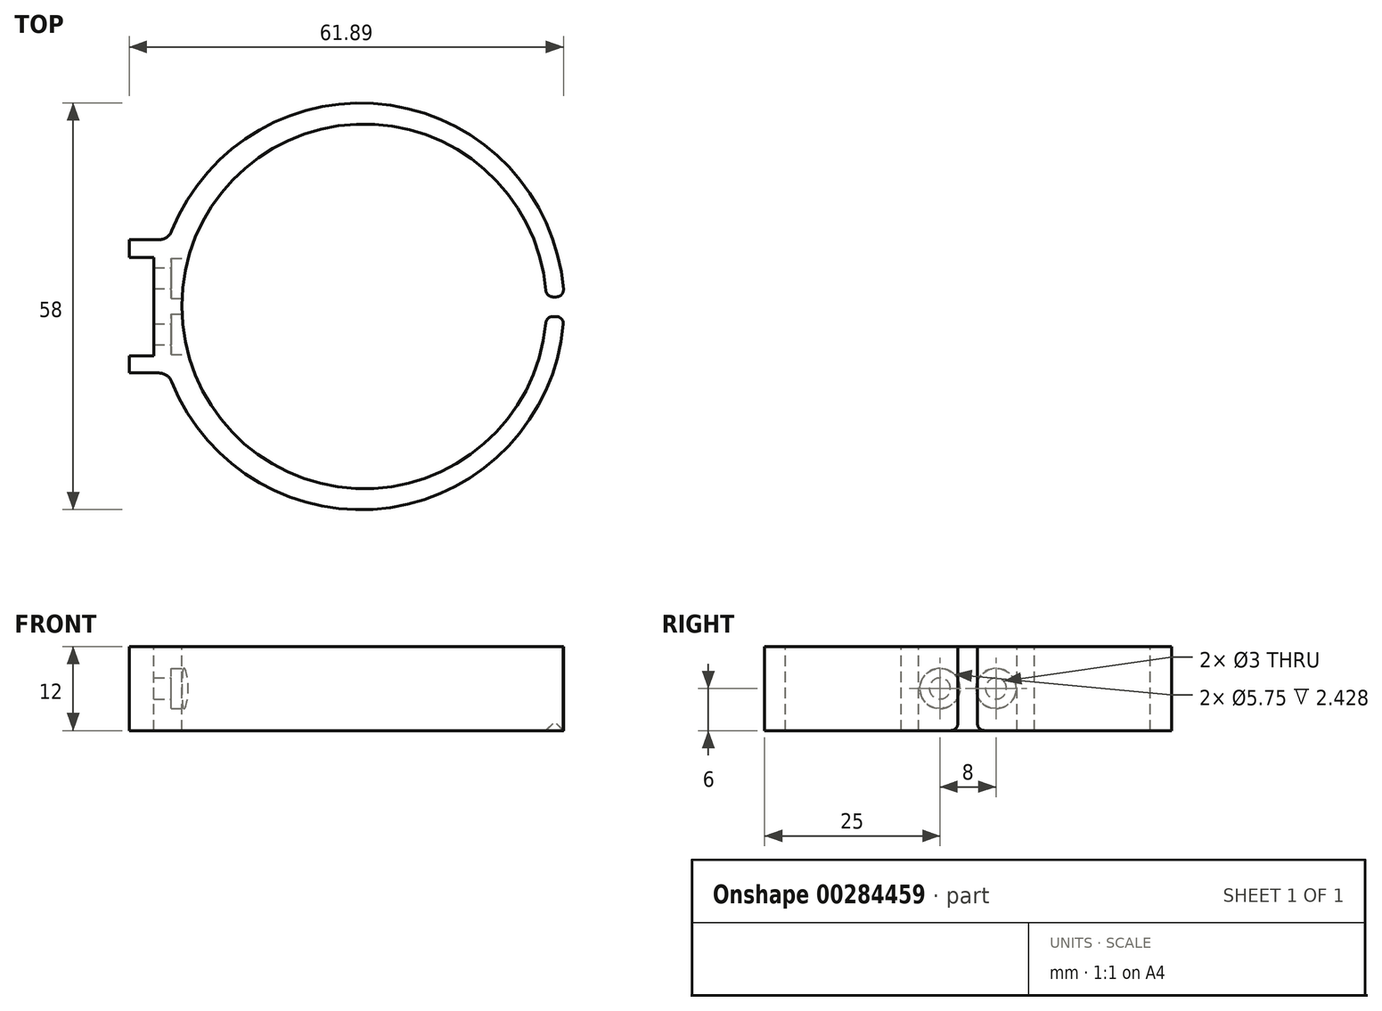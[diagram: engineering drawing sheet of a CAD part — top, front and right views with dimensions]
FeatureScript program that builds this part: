
annotation { "Feature Type Name" : "Feature", "Feature Type Description" : "" }
export const myFeature = defineFeature(function(context is Context, id is Id, definition is map)
    precondition{}
    {
        {
            var Q0;
            Q0=qCreatedBy(makeId("Top.planeOp"),FACE);
            var sketch = newSketch(context, id + "F0", { "sketchPlane" : qUnion([Q0])});
            skCircle(sketch, "E0", {"center": v(0, 0) * mm, "radius": 29 * mm});
            skLineSegment(sketch, "E1.bottom", {"start": v(-33, 9.5) * mm, "end": v(-27, 9.5) * mm});
            skLineSegment(sketch, "E1.top", {"start": v(-33, -9.5) * mm, "end": v(-27, -9.5) * mm});
            skLineSegment(sketch, "E1.left", {"start": v(-33, 9.5) * mm, "end": v(-33, -9.5) * mm});
            skLineSegment(sketch, "E1.right", {"start": v(-27, 9.5) * mm, "end": v(-27, -9.5) * mm});
            skSolve(sketch);
        }
        {
            var Q0;
            Q0 = qSketchRegion(id + "F0", true);
            extrude(context, id + "F1", {"entities" : qUnion([Q0]), "oppositeDirection" : true, "depth" : 12 * mm});
        }
        {
            var Q0;
            Q0=makeQuery(id+"F1.opExtrude","CAP_FACE",FACE,{"disambiguationData":[OSD([sQuery(id+"F0.wireOp",EDGE,"E0")])],"isStart":true});
            var sketch = newSketch(context, id + "F2", { "sketchPlane" : qUnion([Q0])});
            skCircle(sketch, "E2", {"center": v(0.5, 0) * mm, "radius": 26 * mm});
            skLineSegment(sketch, "E3.bottom", {"start": v(25.95, 1.35) * mm, "end": v(29.45, 1.35) * mm});
            skLineSegment(sketch, "E3.top", {"start": v(25.95, -1.45) * mm, "end": v(29.45, -1.45) * mm});
            skLineSegment(sketch, "E3.left", {"start": v(25.95, 1.35) * mm, "end": v(25.95, -1.45) * mm});
            skLineSegment(sketch, "E3.right", {"start": v(29.45, 1.35) * mm, "end": v(29.45, -1.45) * mm});
            skLineSegment(sketch, "E4.bottom", {"start": v(-33, 6.97) * mm, "end": v(-29.5, 6.97) * mm});
            skLineSegment(sketch, "E4.top", {"start": v(-33, -7.03) * mm, "end": v(-29.5, -7.03) * mm});
            skLineSegment(sketch, "E4.left", {"start": v(-33, 6.97) * mm, "end": v(-33, -7.03) * mm});
            skLineSegment(sketch, "E4.right", {"start": v(-29.5, 6.97) * mm, "end": v(-29.5, -7.03) * mm});
            skSolve(sketch);
        }
        {
            var Q0;
            Q0 = qSketchRegion(id + "F2", true);
            extrude(context, id + "F3", {"entities" : qUnion([Q0]), "operationType" : NewBodyOperationType.REMOVE, "oppositeDirection" : true, "depth" : 15 * mm});
        }
        {
            var Q0;
            Q0=makeQuery(id+"F3.boolean.opBoolean","INTERSECT",EDGE,{"derivedFrom":[makeQuery(id+"F1.opExtrude","SWEPT_FACE",FACE,{"disambiguationData":[OSD([sQuery(id+"F0.wireOp",EDGE,"E0")])]}),makeQuery(id+"F3.opExtrude","SWEPT_FACE",FACE,{"disambiguationData":[OSD([sQuery(id+"F2.wireOp",EDGE,"E3.bottom")])]})]});
            var Q1;
            Q1=makeQuery(id+"F3.boolean.opBoolean","INTERSECT",EDGE,{"derivedFrom":[makeQuery(id+"F1.opExtrude","SWEPT_FACE",FACE,{"disambiguationData":[OSD([sQuery(id+"F0.wireOp",EDGE,"E0")])]}),makeQuery(id+"F3.opExtrude","SWEPT_FACE",FACE,{"disambiguationData":[OSD([sQuery(id+"F2.wireOp",EDGE,"E3.top")])]})]});
            var Q2;
            Q2=makeQuery(id+"F3.boolean.opBoolean","COPY",EDGE,{"derivedFrom":makeQuery(id+"F3.opExtrude","SWEPT_EDGE",EDGE,{"disambiguationData":[OSD([sQuery(id+"F2.wireOp",EDGE,"E2"),sQuery(id+"F2.wireOp",EDGE,"E3.bottom")])]})});
            var Q3;
            Q3=makeQuery(id+"F3.boolean.opBoolean","COPY",EDGE,{"derivedFrom":makeQuery(id+"F3.opExtrude","SWEPT_EDGE",EDGE,{"disambiguationData":[OSD([sQuery(id+"F2.wireOp",EDGE,"E2"),sQuery(id+"F2.wireOp",EDGE,"E3.top")])]})});
            var Q4;
            Q4=makeQuery(id+"F3.boolean.opBoolean","COPY",EDGE,{"derivedFrom":makeQuery(id+"F3.opExtrude","CAP_EDGE",EDGE,{"disambiguationData":[OSD([sQuery(id+"F2.wireOp",EDGE,"E3.bottom")])],"isStart":true})});
            var Q5;
            Q5=makeQuery(id+"F3.boolean.opBoolean","COPY",EDGE,{"derivedFrom":makeQuery(id+"F3.opExtrude","CAP_EDGE",EDGE,{"disambiguationData":[OSD([sQuery(id+"F2.wireOp",EDGE,"E3.top")])],"isStart":true})});
            var Q6;
            Q6=makeQuery(id+"F3.boolean.opBoolean","INTERSECT",EDGE,{"derivedFrom":[makeQuery(id+"F1.opExtrude","CAP_FACE",FACE,{"disambiguationData":[OSD([sQuery(id+"F0.wireOp",EDGE,"E0")])],"isStart":false}),makeQuery(id+"F3.opExtrude","SWEPT_FACE",FACE,{"disambiguationData":[OSD([sQuery(id+"F2.wireOp",EDGE,"E3.top")])]})]});
            var Q7;
            Q7=makeQuery(id+"F3.boolean.opBoolean","INTERSECT",EDGE,{"derivedFrom":[makeQuery(id+"F1.opExtrude","CAP_FACE",FACE,{"disambiguationData":[OSD([sQuery(id+"F0.wireOp",EDGE,"E0")])],"isStart":false}),makeQuery(id+"F3.opExtrude","SWEPT_FACE",FACE,{"disambiguationData":[OSD([sQuery(id+"F2.wireOp",EDGE,"E3.bottom")])]})]});
            fillet(context, id + "F4", {"entities" : qUnion([Q0, Q1, Q2, Q3, Q4, Q5, Q6, Q7]), "radius" : 1 * mm, "tangentPropagation" : true, "allowEdgeOverflow" : false});
        }
        {
            var Q0;
            Q0=makeQuery(id+"F1.opExtrude","SWEPT_EDGE",EDGE,{"disambiguationData":[OSD([sQuery(id+"F0.wireOp",EDGE,"E0"),sQuery(id+"F0.wireOp",EDGE,"E1.bottom")])]});
            var Q1;
            Q1=makeQuery(id+"F1.opExtrude","SWEPT_EDGE",EDGE,{"disambiguationData":[OSD([sQuery(id+"F0.wireOp",EDGE,"E0"),sQuery(id+"F0.wireOp",EDGE,"E1.top")])]});
            fillet(context, id + "F5", {"entities" : qUnion([Q0, Q1]), "radius" : 2 * mm, "tangentPropagation" : true, "allowEdgeOverflow" : false});
        }
        {
            var Q0;
            Q0=qCreatedBy(makeId("Right.planeOp"),FACE);
            var sketch = newSketch(context, id + "F6", { "sketchPlane" : qUnion([Q0])});
            skCircle(sketch, "E5", {"center": v(-4, -6) * mm, "radius": 1.5 * mm});
            skLineSegment(sketch, "E6", {"start": v(-4, -6) * mm, "end": v(0, -6) * mm});
            skLineSegment(sketch, "E7", {"start": v(0, -6) * mm, "end": v(4, -6) * mm});
            skCircle(sketch, "E8", {"center": v(4, -6) * mm, "radius": 1.5 * mm});
            skLineSegment(sketch, "E9", {"start": v(0, 0) * mm, "end": v(0, -6) * mm});
            skSolve(sketch);
        }
        {
            var Q0;
            Q0 = qSketchRegion(id + "F6", true);
            extrude(context, id + "F7", {"entities" : qUnion([Q0]), "operationType" : NewBodyOperationType.REMOVE, "oppositeDirection" : true, "depth" : 30 * mm});
        }
        {
            var Q0;
            Q0=qCreatedBy(makeId("Right.planeOp"),FACE);
            var sketch = newSketch(context, id + "F8", { "sketchPlane" : qUnion([Q0])});
            skLineSegment(sketch, "E10", {"start": v(0, 0) * mm, "end": v(0, -6) * mm});
            skLineSegment(sketch, "E11", {"start": v(0, -6) * mm, "end": v(-4, -6) * mm});
            skLineSegment(sketch, "E12", {"start": v(0, -6) * mm, "end": v(4, -6) * mm});
            skCircle(sketch, "E13", {"center": v(-4, -6) * mm, "radius": 2.88 * mm});
            skCircle(sketch, "E14", {"center": v(4, -6) * mm, "radius": 2.88 * mm});
            skSolve(sketch);
        }
        {
            var Q0;
            Q0 = qSketchRegion(id + "F8", true);
            extrude(context, id + "F9", {"entities" : qUnion([Q0]), "operationType" : NewBodyOperationType.REMOVE, "oppositeDirection" : true, "depth" : 27 * mm});
        }
    });
